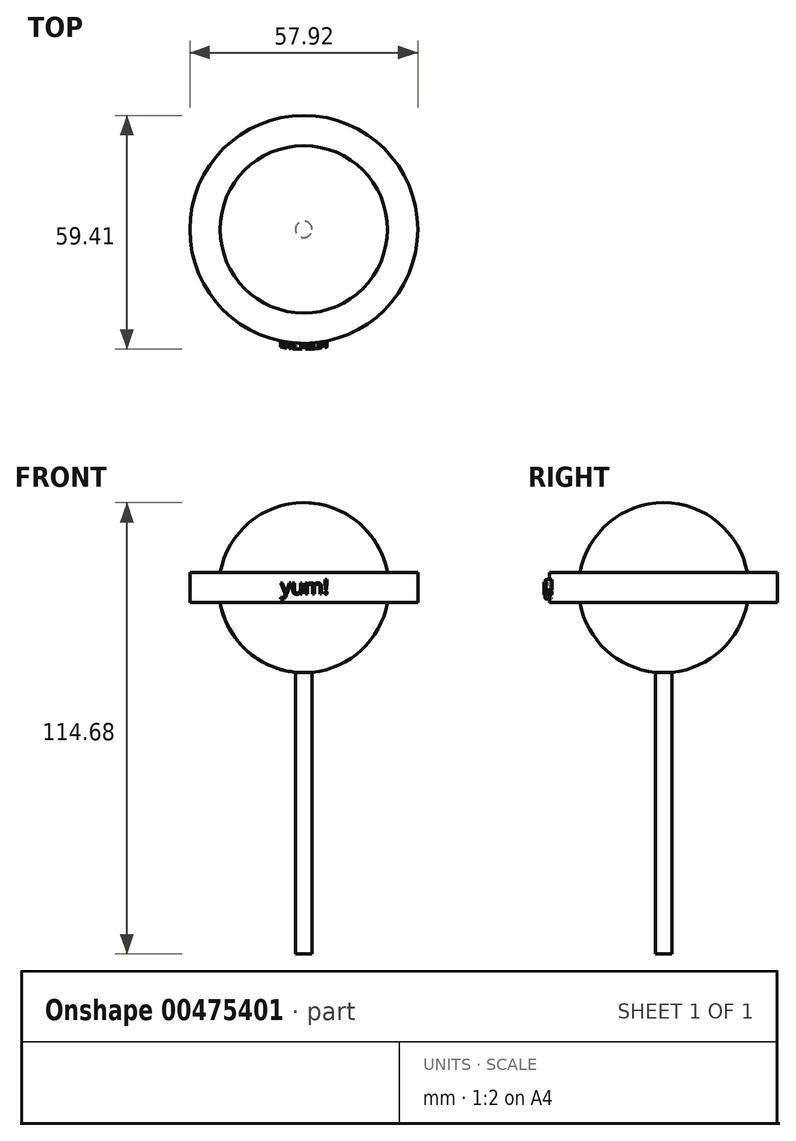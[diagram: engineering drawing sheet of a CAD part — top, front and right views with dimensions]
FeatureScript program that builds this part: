
annotation { "Feature Type Name" : "Feature", "Feature Type Description" : "" }
export const myFeature = defineFeature(function(context is Context, id is Id, definition is map)
    precondition{}
    {
        {
            var Q0;
            Q0=qCreatedBy(makeId("Front.planeOp"),FACE);
            var sketch = newSketch(context, id + "F0", { "sketchPlane" : qUnion([Q0])});
            skArc(sketch, "E0", {"start": v(0, -21.59) * mm, "mid": v(21.59, 0) * mm, "end": v(0, 21.59) * mm});
            skLineSegment(sketch, "E1", {"start": v(0, 21.59) * mm, "end": v(0, -21.59) * mm});
            skLineSegment(sketch, "E2", {"start": v(0, 0) * mm, "end": v(0, 48.31) * mm, "construction": true});
            skLineSegment(sketch, "E3.bottom", {"start": v(28.96, 3.81) * mm, "end": v(5.8, 3.81) * mm});
            skLineSegment(sketch, "E3.top", {"start": v(28.96, -3.81) * mm, "end": v(5.8, -3.81) * mm});
            skLineSegment(sketch, "E3.left", {"start": v(28.96, 3.81) * mm, "end": v(28.96, -3.81) * mm});
            skLineSegment(sketch, "E3.right", {"start": v(5.8, 3.81) * mm, "end": v(5.8, -3.81) * mm});
            skPoint(sketch, "E3.middle", {"position": v(17.37, 0) * mm});
            skLineSegment(sketch, "E4.bottom", {"start": v(0, -17.19) * mm, "end": v(2.1, -17.19) * mm});
            skLineSegment(sketch, "E4.top", {"start": v(0, -93.09) * mm, "end": v(2.1, -93.09) * mm});
            skLineSegment(sketch, "E4.left", {"start": v(0, -17.19) * mm, "end": v(0, -93.09) * mm});
            skLineSegment(sketch, "E4.right", {"start": v(2.1, -17.19) * mm, "end": v(2.1, -93.09) * mm});
            skSolve(sketch);
        }
        {
            var Q0;
            Q0 = qSketchRegion(id + "F0", true);
            var Q1;
            Q1=sQuery(id+"F0.wireOp",EDGE,"E2");
            revolve(context, id + "F1", {"entities" : qUnion([Q0]), "axis" : qUnion([Q1]), "revolveType" : RevolveType.FULL});
        }
        {
            var Q0;
            Q0=qCreatedBy(makeId("Front.planeOp"),FACE);
            var sketch = newSketch(context, id + "F2", { "sketchPlane" : qUnion([Q0])});
            skText(sketch, "E5", { "text": "yum!", "fontName": "OpenSans-Regular.ttf"});
            const initialGuessF2  = {"E5": [-0.0059, -0.00163, 1, 0, 0.00381]};
            skSetInitialGuess(sketch, initialGuessF2);
            skSolve(sketch);
        }
        {
            var Q0;
            Q0 = qSketchRegion(id + "F2", true);
            extrude(context, id + "F3", {"entities" : qUnion([Q0]), "operationType" : NewBodyOperationType.ADD, "depth" : 31.75 * mm});
        }
        {
            var Q0;
            Q0=qCreatedBy(makeId("Front.planeOp"),FACE);
            var sketch = newSketch(context, id + "F4", { "sketchPlane" : qUnion([Q0])});
            skLineSegment(sketch, "E6", {"start": v(28.96, 3.81) * mm, "end": v(28.96, -3.81) * mm});
            skLineSegment(sketch, "E7.0", {"start": v(30.46, -5.31) * mm, "end": v(25.04, -5.31) * mm});
            skLineSegment(sketch, "E7.1", {"start": v(30.46, 5.31) * mm, "end": v(30.46, -5.31) * mm});
            skLineSegment(sketch, "E7.2", {"start": v(30.46, 5.31) * mm, "end": v(21.37, 5.31) * mm});
            skLineSegment(sketch, "E8", {"start": v(21.37, 5.31) * mm, "end": v(18.8, 11.57) * mm});
            skLineSegment(sketch, "E9", {"start": v(18.8, 11.57) * mm, "end": v(31.29, 12.59) * mm});
            skLineSegment(sketch, "E10", {"start": v(31.29, 12.59) * mm, "end": v(40.65, 10.01) * mm});
            skLineSegment(sketch, "E11", {"start": v(40.65, 10.01) * mm, "end": v(40.65, -11.85) * mm});
            skLineSegment(sketch, "E12", {"start": v(40.65, -11.85) * mm, "end": v(26.45, -11.85) * mm});
            skLineSegment(sketch, "E13", {"start": v(26.45, -11.85) * mm, "end": v(25.04, -5.31) * mm});
            skLineSegment(sketch, "E14", {"start": v(0, 0) * mm, "end": v(0, 55.04) * mm, "construction": true});
            skSolve(sketch);
        }
        {
            var Q0;
            Q0 = qSketchRegion(id + "F4", true);
            var Q1;
            Q1=sQuery(id+"F4.wireOp",EDGE,"E14");
            revolve(context, id + "F5", {"operationType" : NewBodyOperationType.REMOVE, "entities" : qUnion([Q0]), "axis" : qUnion([Q1]), "revolveType" : RevolveType.FULL});
        }
    });
